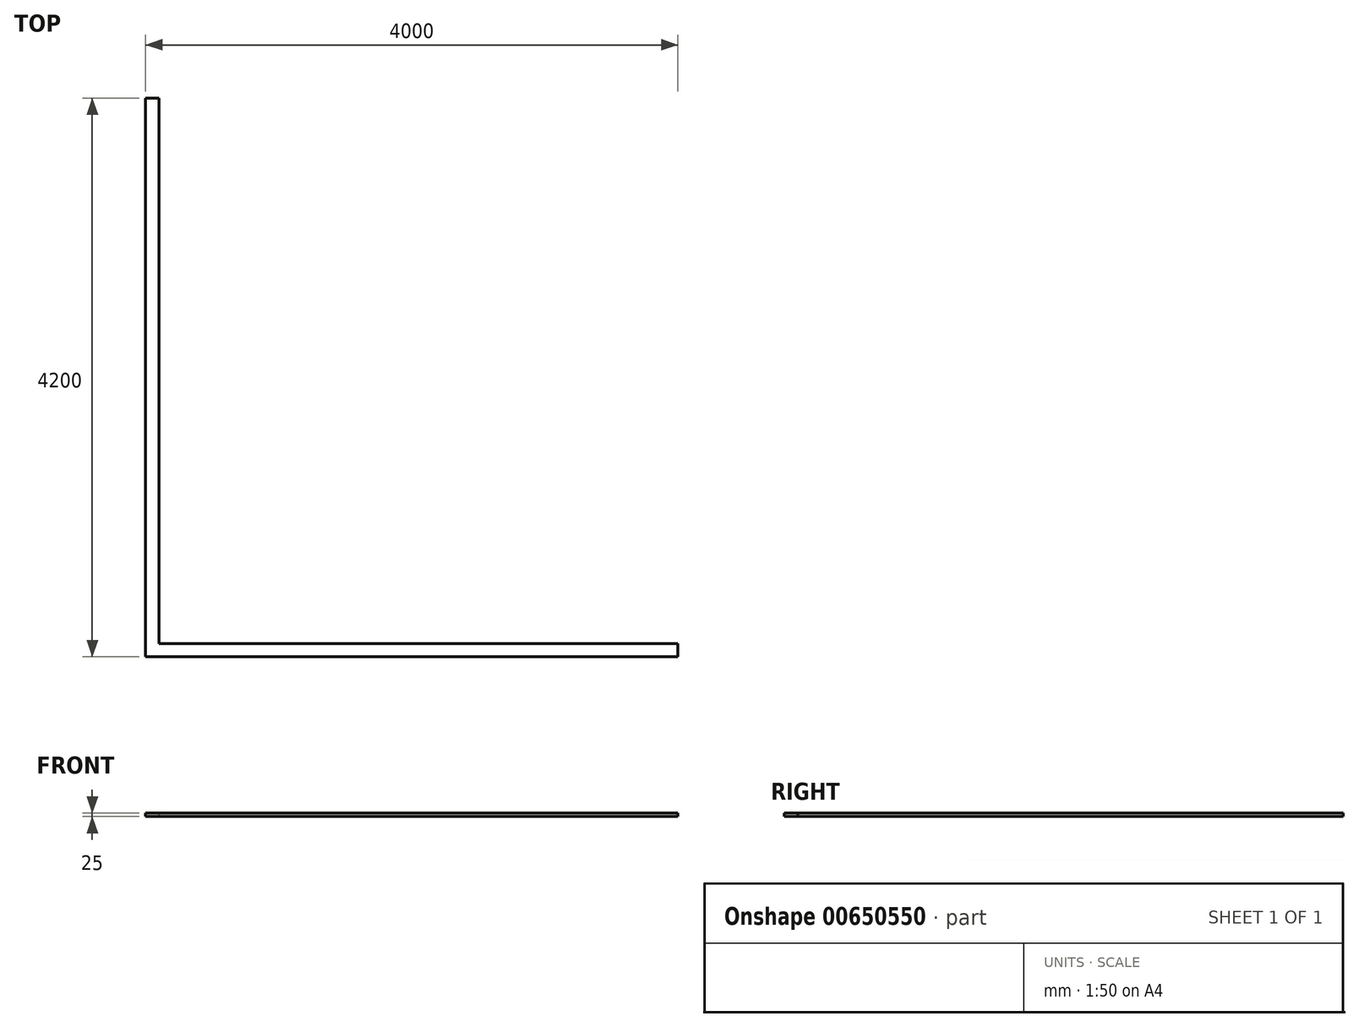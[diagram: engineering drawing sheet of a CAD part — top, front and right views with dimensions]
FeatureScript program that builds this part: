
annotation { "Feature Type Name" : "Feature", "Feature Type Description" : "" }
export const myFeature = defineFeature(function(context is Context, id is Id, definition is map)
    precondition{}
    {
        {
            var Q0;
            Q0=qCreatedBy(makeId("Top.planeOp"),FACE);
            var sketch = newSketch(context, id + "F0", { "sketchPlane" : qUnion([Q0])});
            skLineSegment(sketch, "E0.bottom", {"start": v(0, 0) * mm, "end": v(-4000, 0) * mm});
            skLineSegment(sketch, "E0.top", {"start": v(-3900, 4200) * mm, "end": v(-4000, 4200) * mm});
            skLineSegment(sketch, "E0.left", {"start": v(0, 0) * mm, "end": v(0, 100) * mm});
            skLineSegment(sketch, "E0.right", {"start": v(-4000, 0) * mm, "end": v(-4000, 4200) * mm});
            skLineSegment(sketch, "E1.bottom", {"start": v(0, 100) * mm, "end": v(-3900, 100) * mm});
            skLineSegment(sketch, "E1.right", {"start": v(-3900, 100) * mm, "end": v(-3900, 4200) * mm});
            skSolve(sketch);
        }
        {
            var Q0;
            Q0 = qSketchRegion(id + "F0", true);
            extrude(context, id + "F1", {"entities" : qUnion([Q0]), "depth" : 25 * mm, "offsetDistance" : 25 * mm});
        }
    });
